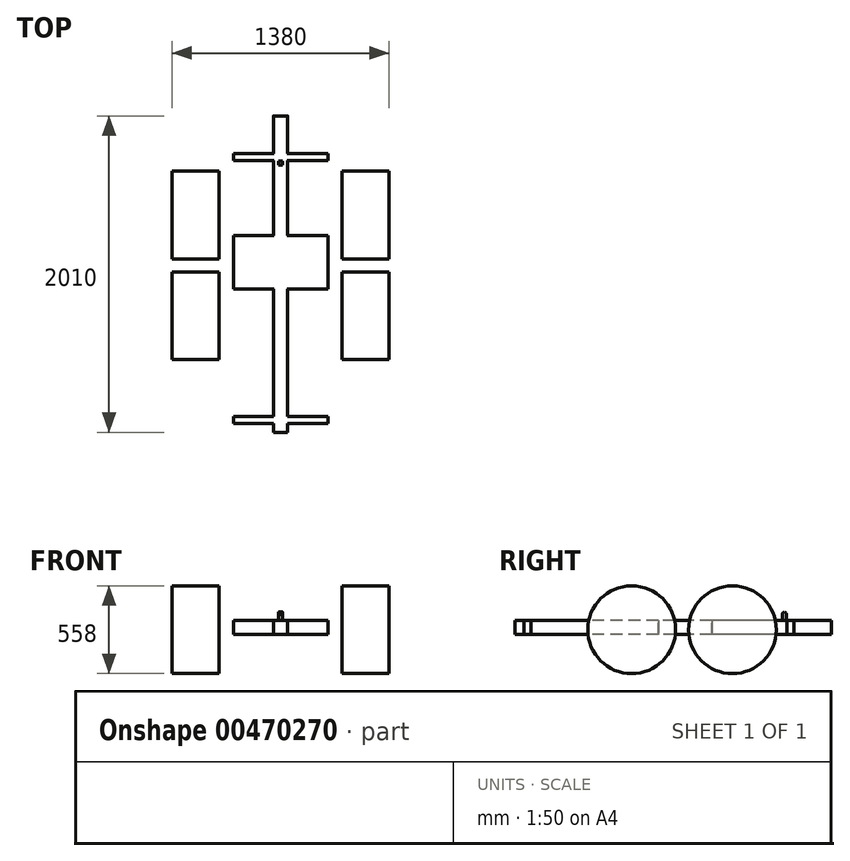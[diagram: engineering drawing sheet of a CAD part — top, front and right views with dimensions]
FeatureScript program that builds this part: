
annotation { "Feature Type Name" : "Feature", "Feature Type Description" : "" }
export const myFeature = defineFeature(function(context is Context, id is Id, definition is map)
    precondition{}
    {
        {
            var Q0;
            Q0=qCreatedBy(makeId("Front.planeOp"),FACE);
            var sketch = newSketch(context, id + "F0", { "sketchPlane" : qUnion([Q0])});
            skLineSegment(sketch, "E0.bottom", {"start": v(45, 0) * mm, "end": v(0, 0) * mm});
            skLineSegment(sketch, "E0.top", {"start": v(45, -90) * mm, "end": v(0, -90) * mm});
            skLineSegment(sketch, "E0.left", {"start": v(45, 0) * mm, "end": v(45, -90) * mm});
            skLineSegment(sketch, "E0.right", {"start": v(0, 0) * mm, "end": v(0, -90) * mm});
            skLineSegment(sketch, "E1.bottom", {"start": v(45, 0) * mm, "end": v(300, 0) * mm});
            skLineSegment(sketch, "E1.top", {"start": v(45, -89.47) * mm, "end": v(300, -89.47) * mm});
            skLineSegment(sketch, "E1.left", {"start": v(45, 0) * mm, "end": v(45, -89.47) * mm});
            skLineSegment(sketch, "E1.right", {"start": v(300, 0) * mm, "end": v(300, -89.47) * mm});
            skSolve(sketch);
        }
        {
            var Q0;
            Q0=makeQuery(id+"F0.imprint","IMPRINT",FACE,{"disambiguationData":[TD([[makeQuery(id+"F0.imprint","IMPRINT",EDGE,{"derivedFrom":sQuery(id+"F0.wireOp",EDGE,"E0.bottom")}),1.0]])]});
            extrude(context, id + "F1", {"entities" : qUnion([Q0]), "oppositeDirection" : true, "depth" : 1800 * mm});
        }
        {
            var Q0;
            Q0=makeQuery(id+"F1.opExtrude","SWEPT_EDGE",EDGE,{"disambiguationData":[OSD([sQuery(id+"F0.wireOp",EDGE,"E0.bottom"),sQuery(id+"F0.wireOp",EDGE,"E1.bottom"),sQuery(id+"F0.wireOp",EDGE,"E1.left")])]});
            var Q1;
            Q1=makeQuery(id+"F1.opExtrude","SWEPT_EDGE",EDGE,{"disambiguationData":[OSD([sQuery(id+"F0.wireOp",EDGE,"E0.top"),sQuery(id+"F0.wireOp",EDGE,"E0.left")])]});
            fillet(context, id + "F2", {"entities" : qUnion([Q0, Q1]), "radius" : 5 * mm, "tangentPropagation" : true, "allowEdgeOverflow" : false});
        }
        {
            var Q0;
            Q0=qCreatedBy(makeId("Top.planeOp"),FACE);
            var sketch = newSketch(context, id + "F3", { "sketchPlane" : qUnion([Q0])});
            skLineSegment(sketch, "E2.bottom", {"start": v(300, 1560) * mm, "end": v(3.85, 1560) * mm});
            skLineSegment(sketch, "E2.top", {"start": v(300, 1515) * mm, "end": v(3.85, 1515) * mm});
            skLineSegment(sketch, "E2.left", {"start": v(300, 1560) * mm, "end": v(300, 1515) * mm});
            skLineSegment(sketch, "E2.right", {"start": v(3.85, 1560) * mm, "end": v(3.85, 1515) * mm});
            skSolve(sketch);
        }
        {
            var Q0;
            Q0=makeQuery(id+"F3.imprint","IMPRINT",FACE,{"disambiguationData":[TD([[makeQuery(id+"F3.imprint","IMPRINT",EDGE,{"derivedFrom":sQuery(id+"F3.wireOp",EDGE,"E2.bottom")}),1.0]])]});
            extrude(context, id + "F4", {"entities" : qUnion([Q0]), "operationType" : NewBodyOperationType.ADD, "oppositeDirection" : true, "depth" : 90 * mm});
        }
        {
            var Q0;
            Q0=qCreatedBy(makeId("Top.planeOp"),FACE);
            var sketch = newSketch(context, id + "F5", { "sketchPlane" : qUnion([Q0])});
            skLineSegment(sketch, "E3.bottom", {"start": v(300, 1040) * mm, "end": v(0, 1040) * mm});
            skLineSegment(sketch, "E3.top", {"start": v(300, 700) * mm, "end": v(0, 700) * mm});
            skLineSegment(sketch, "E3.left", {"start": v(300, 1040) * mm, "end": v(300, 700) * mm});
            skLineSegment(sketch, "E3.right", {"start": v(0, 1040) * mm, "end": v(0, 700) * mm});
            skSolve(sketch);
        }
        {
            var Q0;
            Q0 = qSketchRegion(id + "F5", true);
            extrude(context, id + "F6", {"entities" : qUnion([Q0]), "operationType" : NewBodyOperationType.ADD, "oppositeDirection" : true, "depth" : 90 * mm});
        }
        {
            var Q0;
            Q0=qCreatedBy(makeId("Right.planeOp"),FACE);
            cPlane(context, id + "F7", {"entities" : qUnion([Q0]), "cplaneType" : CPlaneType.OFFSET, "offset" : 690 * mm, "width" : 150 * mm, "height" : 150 * mm});
        }
        {
            var Q0;
            Q0=qCreatedBy(id+"F7.planeOp",FACE);
            var sketch = newSketch(context, id + "F8", { "sketchPlane" : qUnion([Q0])});
            skCircle(sketch, "E4", {"center": v(530, -59) * mm, "radius": 279 * mm});
            skCircle(sketch, "E5.1.0.0", {"center": v(1170, -59) * mm, "radius": 279 * mm});
            skLineSegment(sketch, "E5.direction1", {"start": v(530, -59) * mm, "end": v(1170, -59) * mm, "construction": true});
            skSolve(sketch);
        }
        {
            var Q0;
            Q0 = qSketchRegion(id + "F8", true);
            extrude(context, id + "F9", {"entities" : qUnion([Q0]), "operationType" : NewBodyOperationType.ADD, "oppositeDirection" : true, "depth" : 300 * mm});
        }
        {
            var Q0;
            Q0=makeQuery(id+"F1.opExtrude","SWEPT_BODY",BODY,{"disambiguationData":[OSD([sQuery(id+"F0.wireOp",EDGE,"E0.bottom"),sQuery(id+"F0.wireOp",EDGE,"E0.top"),sQuery(id+"F0.wireOp",EDGE,"E0.left"),sQuery(id+"F0.wireOp",EDGE,"E0.right"),sQuery(id+"F0.wireOp",EDGE,"E1.left")])]});
            var Q1;
            Q1=qCreatedBy(makeId("Right.planeOp"),FACE);
            mirror(context, id + "F10", {"operationType" : NewBodyOperationType.ADD, "entities" : qUnion([Q0]), "mirrorPlane" : qUnion([Q1])});
        }
        {
            var Q0;
            Q0=makeQuery(id+"F9.opExtrude","SWEPT_BODY",BODY,{"disambiguationData":[OSD([sQuery(id+"F8.wireOp",EDGE,"E5.1.0.0")])]});
            var Q1;
            Q1=makeQuery(id+"F9.opExtrude","SWEPT_BODY",BODY,{"disambiguationData":[OSD([sQuery(id+"F8.wireOp",EDGE,"E4")])]});
            var Q2;
            Q2=qCreatedBy(makeId("Right.planeOp"),FACE);
            mirror(context, id + "F11", {"entities" : qUnion([Q0, Q1]), "mirrorPlane" : qUnion([Q2])});
        }
        {
            var Q0;
            Q0=qCreatedBy(makeId("Front.planeOp"),FACE);
            var sketch = newSketch(context, id + "F12", { "sketchPlane" : qUnion([Q0])});
            skLineSegment(sketch, "E6.bottom", {"start": v(0, -90) * mm, "end": v(45, -90) * mm});
            skLineSegment(sketch, "E6.top", {"start": v(0, 0) * mm, "end": v(45, 0) * mm});
            skLineSegment(sketch, "E6.left", {"start": v(0, -90) * mm, "end": v(0, 0) * mm});
            skLineSegment(sketch, "E6.right", {"start": v(45, -90) * mm, "end": v(45, 0) * mm});
            skSolve(sketch);
        }
        {
            var Q0;
            Q0=makeQuery(id+"F12.imprint","IMPRINT",FACE,{"disambiguationData":[TD([[makeQuery(id+"F12.imprint","IMPRINT",EDGE,{"derivedFrom":sQuery(id+"F12.wireOp",EDGE,"E6.bottom")}),1.0]])]});
            extrude(context, id + "F13", {"entities" : qUnion([Q0]), "depth" : 210 * mm});
        }
        {
            var Q0;
            Q0=qCreatedBy(makeId("Right.planeOp"),FACE);
            var sketch = newSketch(context, id + "F14", { "sketchPlane" : qUnion([Q0])});
            skLineSegment(sketch, "E7.bottom", {"start": v(-155, 0) * mm, "end": v(-110, 0) * mm});
            skLineSegment(sketch, "E7.top", {"start": v(-155, -90) * mm, "end": v(-110, -90) * mm});
            skLineSegment(sketch, "E7.left", {"start": v(-155, 0) * mm, "end": v(-155, -90) * mm});
            skLineSegment(sketch, "E7.right", {"start": v(-110, 0) * mm, "end": v(-110, -90) * mm});
            skSolve(sketch);
        }
        {
            var Q0;
            Q0 = qSketchRegion(id + "F14", true);
            extrude(context, id + "F15", {"entities" : qUnion([Q0]), "operationType" : NewBodyOperationType.ADD, "depth" : 300 * mm});
        }
        {
            var Q0;
            Q0=makeQuery(id+"F13.opExtrude","SWEPT_BODY",BODY,{"disambiguationData":[OSD([sQuery(id+"F12.wireOp",EDGE,"E6.bottom"),sQuery(id+"F12.wireOp",EDGE,"E6.top"),sQuery(id+"F12.wireOp",EDGE,"E6.left"),sQuery(id+"F12.wireOp",EDGE,"E6.right")])]});
            var Q1;
            Q1=qCreatedBy(makeId("Right.planeOp"),FACE);
            mirror(context, id + "F16", {"operationType" : NewBodyOperationType.ADD, "entities" : qUnion([Q0]), "mirrorPlane" : qUnion([Q1])});
        }
        {
            var Q0;
            Q0=qCreatedBy(makeId("Right.planeOp"),FACE);
            var sketch = newSketch(context, id + "F17", { "sketchPlane" : qUnion([Q0])});
            skCircle(sketch, "E8", {"center": v(1500, 40) * mm, "radius": 12.5 * mm});
            skLineSegment(sketch, "E9", {"start": v(1487.56, 38.77) * mm, "end": v(1487.56, 0) * mm});
            skLineSegment(sketch, "E10", {"start": v(1487.56, 0) * mm, "end": v(1512.5, 0) * mm});
            skLineSegment(sketch, "E11", {"start": v(1512.5, 0) * mm, "end": v(1512.5, 40) * mm});
            skSolve(sketch);
        }
        {
            var Q0;
            Q0 = qSketchRegion(id + "F17", true);
            extrude(context, id + "F18", {"entities" : qUnion([Q0]), "operationType" : NewBodyOperationType.ADD, "endBound" : BoundingType.SYMMETRIC, "depth" : 25 * mm});
        }
    });
